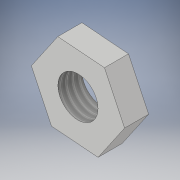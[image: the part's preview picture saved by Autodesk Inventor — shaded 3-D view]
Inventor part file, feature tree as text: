
AUTODESK INVENTOR PART (.ipt)
format: ipt  version: 2019 (Build 230136000, 136)  size: 102,912 bytes
history: native  units: mm
features: extrude x2, sketch x2, thread x1
ambient origin geometry x8: Origin, YZ Plane, XZ Plane, XY Plane, X Axis, Y Axis, Z Axis, Center Point
bodies: Solid1 (feature_tree)
feature tree (5):
  extrude  "Extrusion1"  Depth=3.0mm
  extrude  "Extrusion2"  Depth=10.0mm TaperAngle=0.0deg
  thread  "Thread1"  [1 undecoded]
  sketch  "Sketch1"  dims[d0=3.0mm d1=0.0mm d2=5.0mm]
  sketch  "Sketch2"  dims[d3=3.0mm d4=0.0mm d5=10.0mm d6=0.0mm]
note: 1 required parameter value undecoded (feature->parameter linkage not recoverable at this tier; creation-order binding heuristic only, values carry confidence <= 0.55)
